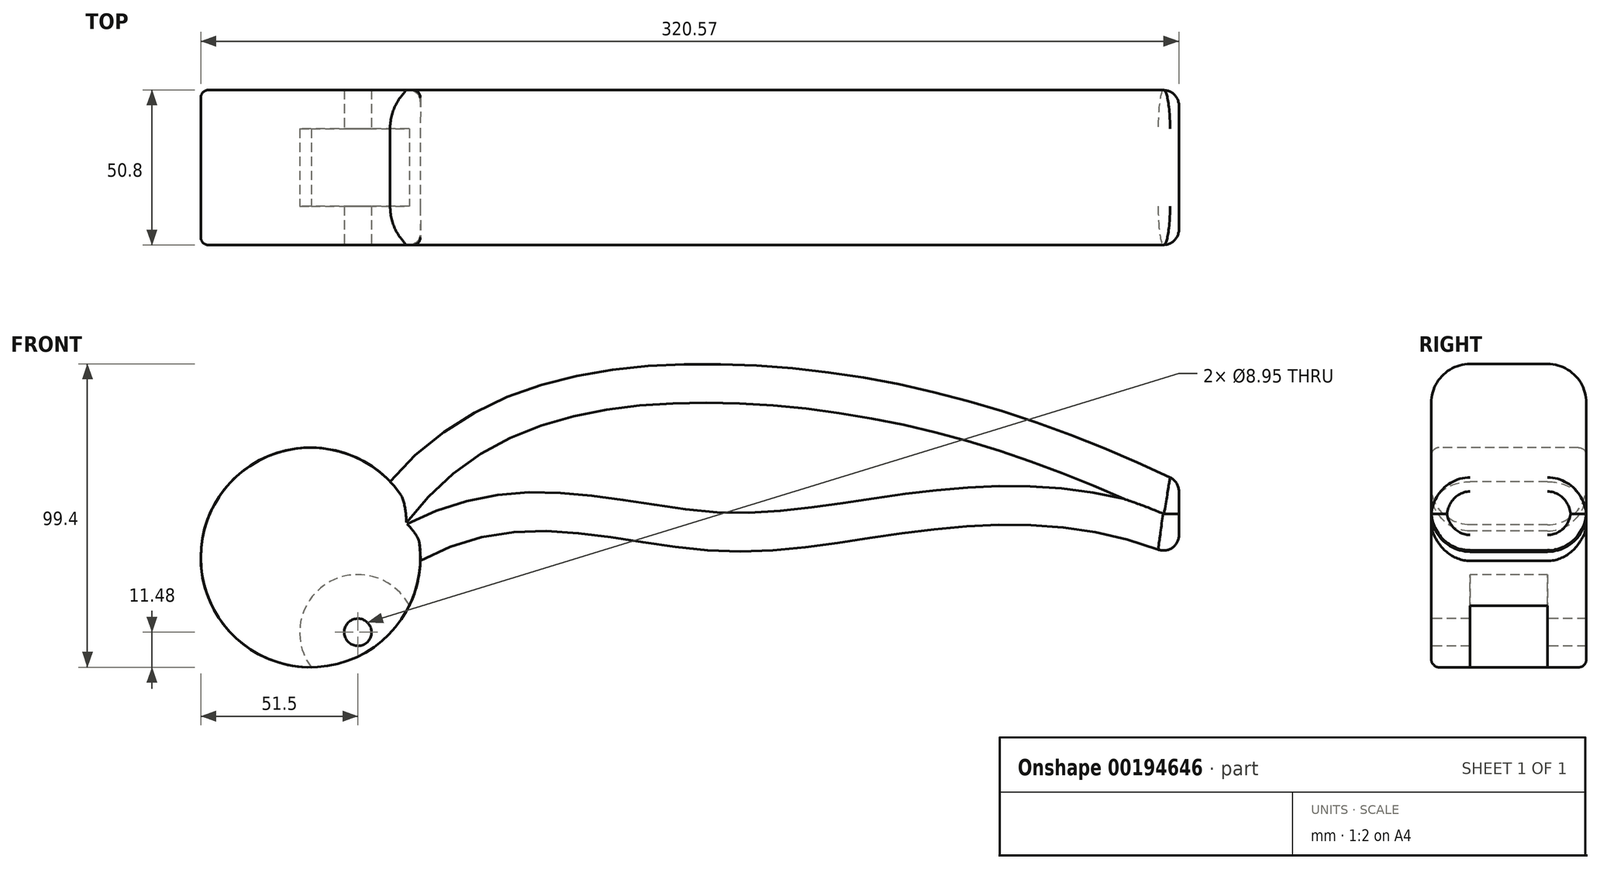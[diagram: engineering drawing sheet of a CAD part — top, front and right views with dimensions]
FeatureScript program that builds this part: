
annotation { "Feature Type Name" : "Feature", "Feature Type Description" : "" }
export const myFeature = defineFeature(function(context is Context, id is Id, definition is map)
    precondition{}
    {
        {
            var Q0;
            Q0=qCreatedBy(makeId("Front.planeOp"),FACE);
            var sketch = newSketch(context, id + "F0", { "sketchPlane" : qUnion([Q0])});
            skFitSpline(sketch, "E0", {"points": [v(-111.26, 0) * mm, v(0, 38.45) * mm, v(147.25, 0) * mm], "startDerivative": vector(175.46, 209) * mm, "endDerivative": vector(290.14, -140.4) * mm});
            skFitSpline(sketch, "E1", {"points": [v(-111.26, -32.31) * mm, v(0, -22.9) * mm, v(147.25, -24.95) * mm], "startDerivative": vector(255.73, 187.18) * mm, "endDerivative": vector(310.72, -133.17) * mm});
            skLineSegment(sketch, "E2", {"start": v(147.25, 0) * mm, "end": v(147.25, -24.95) * mm});
            skArc(sketch, "E3", {"start": v(-111.26, 0) * mm, "mid": v(-170.95, -37.67) * mm, "end": v(-101.35, -25.95) * mm});
            skSolve(sketch);
        }
        {
            var Q0;
            Q0 = qSketchRegion(id + "F0", true);
            extrude(context, id + "F1", {"entities" : qUnion([Q0]), "oppositeDirection" : true, "depth" : 50.8 * mm});
        }
        {
            var Q0;
            Q0=makeQuery(id+"F1.opExtrude","CAP_EDGE",EDGE,{"disambiguationData":[OSD([sQuery(id+"F0.wireOp",EDGE,"E0")])],"isStart":true});
            var Q1;
            Q1=makeQuery(id+"F1.opExtrude","CAP_EDGE",EDGE,{"disambiguationData":[OSD([sQuery(id+"F0.wireOp",EDGE,"E1")])],"isStart":true});
            var Q2;
            Q2=makeQuery(id+"F1.opExtrude","CAP_EDGE",EDGE,{"disambiguationData":[OSD([sQuery(id+"F0.wireOp",EDGE,"E0")])],"isStart":false});
            var Q3;
            Q3=makeQuery(id+"F1.opExtrude","CAP_EDGE",EDGE,{"disambiguationData":[OSD([sQuery(id+"F0.wireOp",EDGE,"E1")])],"isStart":false});
            fillet(context, id + "F2", {"entities" : qUnion([Q0, Q1, Q2, Q3]), "radius" : 12.7 * mm, "tangentPropagation" : true, "allowEdgeOverflow" : false});
        }
        {
            var Q0;
            Q0=qCreatedBy(makeId("Front.planeOp"),FACE);
            var sketch = newSketch(context, id + "F3", { "sketchPlane" : qUnion([Q0])});
            skCircle(sketch, "E4", {"center": v(-121.82, -49.34) * mm, "radius": 4.48 * mm});
            skSolve(sketch);
        }
        {
            var Q0;
            Q0 = qSketchRegion(id + "F3", true);
            extrude(context, id + "F4", {"entities" : qUnion([Q0]), "operationType" : NewBodyOperationType.REMOVE, "endBound" : BoundingType.THROUGH_ALL, "oppositeDirection" : true, "depth" : 55.37 * mm});
        }
        {
            var Q0;
            Q0=makeQuery(id+"F1.opExtrude","SWEPT_FACE",FACE,{"disambiguationData":[OSD([sQuery(id+"F0.wireOp",EDGE,"E2")])]});
            fillet(context, id + "F5", {"entities" : qUnion([Q0]), "radius" : 5.08 * mm, "tangentPropagation" : true, "allowEdgeOverflow" : false});
        }
        {
            var Q0;
            Q0=makeQuery(id+"F1.opExtrude","CAP_EDGE",EDGE,{"disambiguationData":[OSD([sQuery(id+"F0.wireOp",EDGE,"E3")])],"isStart":true});
            var Q1;
            Q1=makeQuery(id+"F1.opExtrude","CAP_EDGE",EDGE,{"disambiguationData":[OSD([sQuery(id+"F0.wireOp",EDGE,"E3")])],"isStart":false});
            fillet(context, id + "F6", {"entities" : qUnion([Q0, Q1]), "radius" : 2.54 * mm, "tangentPropagation" : true, "allowEdgeOverflow" : false});
        }
        {
            var Q0;
            Q0=qCreatedBy(makeId("Front.planeOp"),FACE);
            cPlane(context, id + "F7", {"entities" : qUnion([Q0]), "cplaneType" : CPlaneType.OFFSET, "offset" : 25.4 * mm, "oppositeDirection" : true, "width" : 152.4 * mm, "height" : 152.4 * mm});
        }
        {
            var Q0;
            Q0=qCreatedBy(id+"F7.planeOp",FACE);
            var sketch = newSketch(context, id + "F8", { "sketchPlane" : qUnion([Q0])});
            skCircle(sketch, "E5", {"center": v(-121.84, -49.48) * mm, "radius": 19.05 * mm});
            skSolve(sketch);
        }
        {
            var Q0;
            Q0 = qSketchRegion(id + "F8", true);
            extrude(context, id + "F9", {"entities" : qUnion([Q0]), "operationType" : NewBodyOperationType.REMOVE, "endBound" : BoundingType.SYMMETRIC, "oppositeDirection" : true, "depth" : 25.4 * mm});
        }
    });
